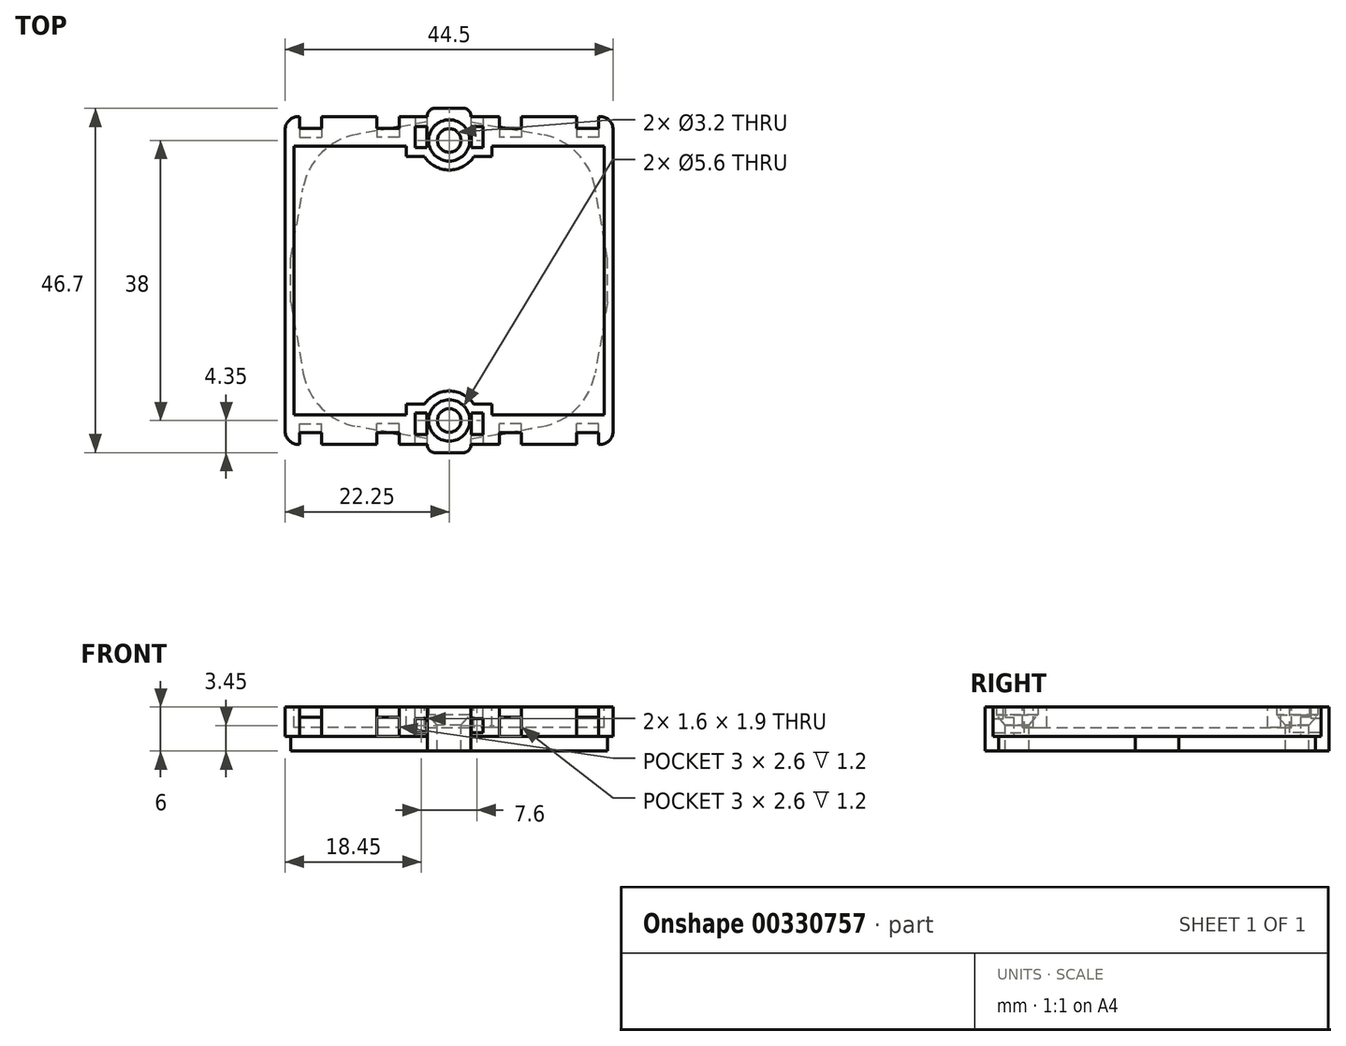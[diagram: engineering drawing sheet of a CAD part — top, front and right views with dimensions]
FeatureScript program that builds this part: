
annotation { "Feature Type Name" : "Feature", "Feature Type Description" : "" }
export const myFeature = defineFeature(function(context is Context, id is Id, definition is map)
    precondition{}
    {
        {
            var Q0;
            Q0=qCreatedBy(makeId("Top.planeOp"),FACE);
            var sketch = newSketch(context, id + "F0", { "sketchPlane" : qUnion([Q0])});
            skLineSegment(sketch, "E0.bottom", {"start": v(4.95, 0) * mm, "end": v(12.45, 0) * mm});
            skLineSegment(sketch, "E0.top", {"start": v(4.95, 44.5) * mm, "end": v(12.45, 44.5) * mm});
            skLineSegment(sketch, "E0.left", {"start": v(0, 1.8) * mm, "end": v(0, 42.7) * mm});
            skLineSegment(sketch, "E0.right", {"start": v(44.5, 1.8) * mm, "end": v(44.5, 42.7) * mm});
            skPoint(sketch, "E1.visualSharp", {"position": v(0, 44.5) * mm});
            skArc(sketch, "E1.filletArc", {"start": v(1.8, 44.5) * mm, "mid": v(0.53, 43.97) * mm, "end": v(0, 42.7) * mm});
            skPoint(sketch, "E2.visualSharp", {"position": v(44.5, 44.5) * mm});
            skArc(sketch, "E2.filletArc", {"start": v(44.5, 42.7) * mm, "mid": v(43.97, 43.97) * mm, "end": v(42.7, 44.5) * mm});
            skPoint(sketch, "E3.visualSharp", {"position": v(44.5, 0) * mm});
            skArc(sketch, "E3.filletArc", {"start": v(42.7, 0) * mm, "mid": v(43.97, 0.53) * mm, "end": v(44.5, 1.8) * mm});
            skPoint(sketch, "E4.visualSharp", {"position": v(0, 0) * mm});
            skArc(sketch, "E4.filletArc", {"start": v(0, 1.8) * mm, "mid": v(0.53, 0.53) * mm, "end": v(1.8, 0) * mm});
            skLineSegment(sketch, "E5.bottom", {"start": v(19.3, 1.1) * mm, "end": v(25.2, 1.1) * mm});
            skLineSegment(sketch, "E5.top", {"start": v(19.3, -1.1) * mm, "end": v(25.2, -1.1) * mm});
            skLineSegment(sketch, "E5.left", {"start": v(19.3, 1.1) * mm, "end": v(19.3, -1.1) * mm});
            skLineSegment(sketch, "E5.right", {"start": v(25.2, 1.1) * mm, "end": v(25.2, -1.1) * mm});
            skPoint(sketch, "E5.middle", {"position": v(22.25, 0) * mm});
            skLineSegment(sketch, "E6.bottom", {"start": v(19.3, 45.6) * mm, "end": v(25.2, 45.6) * mm});
            skLineSegment(sketch, "E6.top", {"start": v(19.3, 43.4) * mm, "end": v(25.2, 43.4) * mm});
            skLineSegment(sketch, "E6.left", {"start": v(19.3, 45.6) * mm, "end": v(19.3, 43.4) * mm});
            skLineSegment(sketch, "E6.right", {"start": v(25.2, 45.6) * mm, "end": v(25.2, 43.4) * mm});
            skPoint(sketch, "E6.middle", {"position": v(22.25, 44.5) * mm});
            skLineSegment(sketch, "E7.bottom", {"start": v(1.8, 0) * mm, "end": v(1.95, 0) * mm});
            skLineSegment(sketch, "E7.top", {"start": v(1.95, 1.6) * mm, "end": v(4.95, 1.6) * mm});
            skLineSegment(sketch, "E7.left", {"start": v(1.95, 0) * mm, "end": v(1.95, 1.6) * mm});
            skLineSegment(sketch, "E7.right", {"start": v(4.95, 0) * mm, "end": v(4.95, 1.6) * mm});
            skPoint(sketch, "E8.oppositeSnap0", {"position": v(3.45, 1.6) * mm});
            skLineSegment(sketch, "E8.top", {"start": v(12.45, 1.6) * mm, "end": v(15.45, 1.6) * mm});
            skLineSegment(sketch, "E8.left", {"start": v(12.45, 0) * mm, "end": v(12.45, 1.6) * mm});
            skLineSegment(sketch, "E8.right", {"start": v(15.45, 0) * mm, "end": v(15.45, 1.6) * mm});
            skLineSegment(sketch, "E9", {"start": v(22.25, 0) * mm, "end": v(22.25, 44.5) * mm, "construction": true});
            skLineSegment(sketch, "E10", {"start": v(44.5, 22.25) * mm, "end": v(0, 22.25) * mm, "construction": true});
            skLineSegment(sketch, "E11.MirrorCS", {"start": v(1.95, 44.5) * mm, "end": v(1.95, 42.9) * mm});
            skLineSegment(sketch, "E12.MirrorCS", {"start": v(1.95, 42.9) * mm, "end": v(4.95, 42.9) * mm});
            skLineSegment(sketch, "E13.MirrorCS", {"start": v(4.95, 44.5) * mm, "end": v(4.95, 42.9) * mm});
            skLineSegment(sketch, "E14.MirrorCS", {"start": v(12.45, 44.5) * mm, "end": v(12.45, 42.9) * mm});
            skLineSegment(sketch, "E15.MirrorCS", {"start": v(12.45, 42.9) * mm, "end": v(15.45, 42.9) * mm});
            skLineSegment(sketch, "E16.MirrorCS", {"start": v(15.45, 44.5) * mm, "end": v(15.45, 42.9) * mm});
            skLineSegment(sketch, "E17.MirrorCS", {"start": v(29.05, 0) * mm, "end": v(29.05, 1.6) * mm});
            skLineSegment(sketch, "E18.MirrorCS", {"start": v(32.05, 1.6) * mm, "end": v(29.05, 1.6) * mm});
            skLineSegment(sketch, "E19.MirrorCS", {"start": v(32.05, 0) * mm, "end": v(32.05, 1.6) * mm});
            skLineSegment(sketch, "E20.MirrorCS", {"start": v(39.55, 0) * mm, "end": v(39.55, 1.6) * mm});
            skLineSegment(sketch, "E21.MirrorCS", {"start": v(42.55, 1.6) * mm, "end": v(39.55, 1.6) * mm});
            skLineSegment(sketch, "E22.MirrorCS", {"start": v(42.55, 0) * mm, "end": v(42.55, 1.6) * mm});
            skLineSegment(sketch, "E23.MirrorCS", {"start": v(42.55, 44.5) * mm, "end": v(42.55, 42.9) * mm});
            skLineSegment(sketch, "E24.MirrorCS", {"start": v(42.55, 42.9) * mm, "end": v(39.55, 42.9) * mm});
            skLineSegment(sketch, "E25.MirrorCS", {"start": v(39.55, 44.5) * mm, "end": v(39.55, 42.9) * mm});
            skLineSegment(sketch, "E26.MirrorCS", {"start": v(32.05, 44.5) * mm, "end": v(32.05, 42.9) * mm});
            skLineSegment(sketch, "E27.MirrorCS", {"start": v(32.05, 42.9) * mm, "end": v(29.05, 42.9) * mm});
            skLineSegment(sketch, "E28.MirrorCS", {"start": v(29.05, 44.5) * mm, "end": v(29.05, 42.9) * mm});
            skLineSegment(sketch, "E29.trimOffspring", {"start": v(15.45, 0) * mm, "end": v(29.05, 0) * mm});
            skLineSegment(sketch, "E30.trimOffspring", {"start": v(32.05, 0) * mm, "end": v(39.55, 0) * mm});
            skLineSegment(sketch, "E31.trimOffspring", {"start": v(32.05, 44.5) * mm, "end": v(39.55, 44.5) * mm});
            skLineSegment(sketch, "E32.trimOffspring", {"start": v(15.45, 44.5) * mm, "end": v(29.05, 44.5) * mm});
            skLineSegment(sketch, "E33", {"start": v(1.8, 44.5) * mm, "end": v(1.95, 44.5) * mm});
            skLineSegment(sketch, "E34", {"start": v(42.55, 44.5) * mm, "end": v(42.7, 44.5) * mm});
            skLineSegment(sketch, "E35", {"start": v(42.55, 0) * mm, "end": v(42.7, 0) * mm});
            skSolve(sketch);
        }
        {
            var Q0;
            Q0 = qSketchRegion(id + "F0", true);
            extrude(context, id + "F1", {"entities" : qUnion([Q0]), "depth" : (4.5 - 1.6) * mm, "offsetDistance" : 25 * mm});
        }
        {
            var Q0;
            Q0=makeQuery(id+"F1.opExtrude","CAP_FACE",FACE,{"disambiguationData":[OSD([sQuery(id+"F0.wireOp",EDGE,"E0.bottom"),sQuery(id+"F0.wireOp",EDGE,"E0.top"),sQuery(id+"F0.wireOp",EDGE,"E0.left"),sQuery(id+"F0.wireOp",EDGE,"E0.right"),sQuery(id+"F0.wireOp",EDGE,"E1.filletArc"),sQuery(id+"F0.wireOp",EDGE,"E2.filletArc"),sQuery(id+"F0.wireOp",EDGE,"E3.filletArc"),sQuery(id+"F0.wireOp",EDGE,"E4.filletArc")])],"isStart":true});
            var sketch = newSketch(context, id + "F2", { "sketchPlane" : qUnion([Q0])});
            skLineSegment(sketch, "E36.bottom", {"start": v(19.3, -0.75) * mm, "end": v(25.2, -0.75) * mm});
            skLineSegment(sketch, "E36.top", {"start": v(19.3, -43.75) * mm, "end": v(25.2, -43.75) * mm});
            skLineSegment(sketch, "E36.left", {"start": v(19.3, -0.75) * mm, "end": v(19.3, -43.75) * mm, "construction": true});
            skLineSegment(sketch, "E36.right", {"start": v(25.2, -0.75) * mm, "end": v(25.2, -43.75) * mm, "construction": true});
            skLineSegment(sketch, "E37.bottom", {"start": v(0.75, -19.3) * mm, "end": v(43.75, -19.3) * mm, "construction": true});
            skLineSegment(sketch, "E37.top", {"start": v(0.75, -25.2) * mm, "end": v(43.75, -25.2) * mm, "construction": true});
            skLineSegment(sketch, "E37.left", {"start": v(0.75, -19.3) * mm, "end": v(0.75, -25.2) * mm});
            skLineSegment(sketch, "E37.right", {"start": v(43.75, -19.3) * mm, "end": v(43.75, -25.2) * mm});
            skPoint(sketch, "E38", {"position": v(22.25, -22.25) * mm});
            skPoint(sketch, "E38.positionSnap0", {"position": v(19.3, -22.25) * mm});
            skPoint(sketch, "E38.positionSnap1", {"position": v(22.25, -25.2) * mm});
            skLineSegment(sketch, "E39", {"start": v(22.25, -22.25) * mm, "end": v(0, 0) * mm, "construction": true});
            skLineSegment(sketch, "E40", {"start": v(22.25, -22.25) * mm, "end": v(43.97, -43.97) * mm, "construction": true});
            skLineSegment(sketch, "E41", {"start": v(22.25, -22.25) * mm, "end": v(41.34, -3.16) * mm, "construction": true});
            skLineSegment(sketch, "E42", {"start": v(22.25, -22.25) * mm, "end": v(5.04, -39.46) * mm, "construction": true});
            skArc(sketch, "E43", {"start": v(9.74, -2.42) * mm, "mid": v(4.93, -4.93) * mm, "end": v(2.42, -9.74) * mm});
            skArc(sketch, "E44", {"start": v(42.08, -9.74) * mm, "mid": v(39.57, -4.93) * mm, "end": v(34.76, -2.42) * mm});
            skArc(sketch, "E45", {"start": v(34.76, -42.08) * mm, "mid": v(39.57, -39.57) * mm, "end": v(42.08, -34.76) * mm});
            skArc(sketch, "E46", {"start": v(2.42, -34.76) * mm, "mid": v(4.93, -39.57) * mm, "end": v(9.74, -42.08) * mm});
            skLineSegment(sketch, "E47", {"start": v(19.3, -0.75) * mm, "end": v(9.74, -2.42) * mm});
            skLineSegment(sketch, "E48", {"start": v(0.75, -19.3) * mm, "end": v(2.42, -9.74) * mm});
            skLineSegment(sketch, "E49", {"start": v(0.75, -25.2) * mm, "end": v(2.42, -34.76) * mm});
            skLineSegment(sketch, "E50", {"start": v(19.3, -43.75) * mm, "end": v(9.74, -42.08) * mm});
            skLineSegment(sketch, "E51", {"start": v(25.2, -43.75) * mm, "end": v(34.76, -42.08) * mm});
            skLineSegment(sketch, "E52", {"start": v(43.75, -25.2) * mm, "end": v(42.08, -34.76) * mm});
            skLineSegment(sketch, "E53", {"start": v(43.75, -19.3) * mm, "end": v(42.08, -9.74) * mm});
            skLineSegment(sketch, "E54", {"start": v(25.2, -0.75) * mm, "end": v(34.76, -2.42) * mm});
            skLineSegment(sketch, "E55.0", {"start": v(19.3, 1.1) * mm, "end": v(25.2, 1.1) * mm});
            skLineSegment(sketch, "E56", {"start": v(25.2, 1.1) * mm, "end": v(25.2, -0.75) * mm});
            skLineSegment(sketch, "E57", {"start": v(19.3, 1.1) * mm, "end": v(19.3, -0.75) * mm});
            skLineSegment(sketch, "E58.0", {"start": v(19.3, -45.6) * mm, "end": v(25.2, -45.6) * mm});
            skLineSegment(sketch, "E59", {"start": v(19.3, -43.75) * mm, "end": v(19.3, -45.6) * mm});
            skLineSegment(sketch, "E60", {"start": v(25.2, -43.75) * mm, "end": v(25.2, -45.6) * mm});
            skSolve(sketch);
        }
        {
            var Q0;
            Q0 = qSketchRegion(id + "F2", true);
            extrude(context, id + "F3", {"entities" : qUnion([Q0]), "operationType" : NewBodyOperationType.ADD, "depth" : 2 * mm, "offsetDistance" : 25 * mm});
        }
        {
            var Q0;
            Q0=makeQuery(id+"F1.opExtrude","CAP_FACE",FACE,{"disambiguationData":[OSD([sQuery(id+"F0.wireOp",EDGE,"E0.bottom"),sQuery(id+"F0.wireOp",EDGE,"E0.top"),sQuery(id+"F0.wireOp",EDGE,"E0.left"),sQuery(id+"F0.wireOp",EDGE,"E0.right"),sQuery(id+"F0.wireOp",EDGE,"E1.filletArc"),sQuery(id+"F0.wireOp",EDGE,"E2.filletArc"),sQuery(id+"F0.wireOp",EDGE,"E3.filletArc"),sQuery(id+"F0.wireOp",EDGE,"E4.filletArc"),sQuery(id+"F0.wireOp",EDGE,"E5.top"),sQuery(id+"F0.wireOp",EDGE,"E5.left"),sQuery(id+"F0.wireOp",EDGE,"E5.right"),sQuery(id+"F0.wireOp",EDGE,"E6.bottom"),sQuery(id+"F0.wireOp",EDGE,"E6.left"),sQuery(id+"F0.wireOp",EDGE,"E6.right")])],"isStart":false});
            var sketch = newSketch(context, id + "F4", { "sketchPlane" : qUnion([Q0])});
            skLineSegment(sketch, "E61", {"start": v(22.25, 45.6) * mm, "end": v(22.25, -1.1) * mm, "construction": true});
            skPoint(sketch, "E62", {"position": v(22.25, 41.25) * mm});
            skPoint(sketch, "E63", {"position": v(22.25, 3.25) * mm});
            skPoint(sketch, "E64", {"position": v(22.25, 22.25) * mm});
            skSolve(sketch);
        }
        {
            var Q0;
            Q0=sQuery(id+"F4.wireOp",VERTEX,"E62");
            var Q1;
            Q1=sQuery(id+"F4.wireOp",VERTEX,"E63");
            var Q2;
            Q2=makeQuery(id+"F1.opExtrude","SWEPT_BODY",BODY,{"disambiguationData":[OSD([sQuery(id+"F0.wireOp",EDGE,"E0.bottom"),sQuery(id+"F0.wireOp",EDGE,"E0.top"),sQuery(id+"F0.wireOp",EDGE,"E0.left"),sQuery(id+"F0.wireOp",EDGE,"E0.right"),sQuery(id+"F0.wireOp",EDGE,"E1.filletArc"),sQuery(id+"F0.wireOp",EDGE,"E2.filletArc"),sQuery(id+"F0.wireOp",EDGE,"E3.filletArc"),sQuery(id+"F0.wireOp",EDGE,"E4.filletArc"),sQuery(id+"F0.wireOp",EDGE,"E5.top"),sQuery(id+"F0.wireOp",EDGE,"E5.left"),sQuery(id+"F0.wireOp",EDGE,"E5.right"),sQuery(id+"F0.wireOp",EDGE,"E6.bottom"),sQuery(id+"F0.wireOp",EDGE,"E6.left"),sQuery(id+"F0.wireOp",EDGE,"E6.right")])]});
            hole(context, id + "F5", {"style" : HoleStyle.C_SINK, "endStyle" : HoleEndStyle.THROUGH, "holeDiameter" : 3.2 * mm, "cSinkDiameter" : 5.6 * mm, "cSinkAngle" : 82 * degree, "majorDiameter" : 5 * mm, "isTappedThrough" : true, "tappedDepth" : 12 * mm, "tapClearance" : 3, "locations" : qUnion([Q0, Q1]), "scope" : qUnion([Q2])});
        }
        {
            var Q0;
            Q0=makeQuery(id+"F1.opExtrude","CAP_FACE",FACE,{"disambiguationData":[OSD([sQuery(id+"F0.wireOp",EDGE,"E0.bottom"),sQuery(id+"F0.wireOp",EDGE,"E0.top"),sQuery(id+"F0.wireOp",EDGE,"E0.left"),sQuery(id+"F0.wireOp",EDGE,"E0.right"),sQuery(id+"F0.wireOp",EDGE,"E1.filletArc"),sQuery(id+"F0.wireOp",EDGE,"E2.filletArc"),sQuery(id+"F0.wireOp",EDGE,"E3.filletArc"),sQuery(id+"F0.wireOp",EDGE,"E4.filletArc"),sQuery(id+"F0.wireOp",EDGE,"E5.top"),sQuery(id+"F0.wireOp",EDGE,"E5.left"),sQuery(id+"F0.wireOp",EDGE,"E5.right"),sQuery(id+"F0.wireOp",EDGE,"E6.bottom"),sQuery(id+"F0.wireOp",EDGE,"E6.left"),sQuery(id+"F0.wireOp",EDGE,"E6.right")])],"isStart":false});
            extrude(context, id + "F6", {"entities" : qUnion([Q0]), "operationType" : NewBodyOperationType.ADD, "depth" : 1.1 * mm, "offsetDistance" : 25 * mm});
        }
        {
            var Q0;
            {var subQ0=sQuery(id+"F0.wireOp",EDGE,"E5.right");var subQ1=sQuery(id+"F0.wireOp",EDGE,"E5.top");Q0=makeQuery(id+"F6.boolean.opBoolean","MERGE",EDGE,{"derivedFrom":[makeQuery(id+"F3.boolean.opBoolean","MERGE",EDGE,{"derivedFrom":[makeQuery(id+"F1.opExtrude","SWEPT_EDGE",EDGE,{"disambiguationData":[OSD([subQ1,subQ0])]}),makeQuery(id+"F3.opExtrude","SWEPT_EDGE",EDGE,{"disambiguationData":[OSD([sQuery(id+"F2.wireOp",EDGE,"E55.0"),sQuery(id+"F2.wireOp",EDGE,"E56")])]})]}),makeQuery(id+"F6.opExtrude","SWEPT_EDGE",EDGE,{"disambiguationData":[OSD([subQ1,subQ0])]})]});}
            var Q1;
            {var subQ0=sQuery(id+"F0.wireOp",EDGE,"E5.left");var subQ1=sQuery(id+"F0.wireOp",EDGE,"E5.top");Q1=makeQuery(id+"F6.boolean.opBoolean","MERGE",EDGE,{"derivedFrom":[makeQuery(id+"F3.boolean.opBoolean","MERGE",EDGE,{"derivedFrom":[makeQuery(id+"F1.opExtrude","SWEPT_EDGE",EDGE,{"disambiguationData":[OSD([subQ1,subQ0])]}),makeQuery(id+"F3.opExtrude","SWEPT_EDGE",EDGE,{"disambiguationData":[OSD([sQuery(id+"F2.wireOp",EDGE,"E55.0"),sQuery(id+"F2.wireOp",EDGE,"E57")])]})]}),makeQuery(id+"F6.opExtrude","SWEPT_EDGE",EDGE,{"disambiguationData":[OSD([subQ1,subQ0])]})]});}
            var Q2;
            {var subQ0=sQuery(id+"F0.wireOp",EDGE,"E6.right");var subQ1=sQuery(id+"F0.wireOp",EDGE,"E6.bottom");Q2=makeQuery(id+"F6.boolean.opBoolean","MERGE",EDGE,{"derivedFrom":[makeQuery(id+"F3.boolean.opBoolean","MERGE",EDGE,{"derivedFrom":[makeQuery(id+"F1.opExtrude","SWEPT_EDGE",EDGE,{"disambiguationData":[OSD([subQ1,subQ0])]}),makeQuery(id+"F3.opExtrude","SWEPT_EDGE",EDGE,{"disambiguationData":[OSD([sQuery(id+"F2.wireOp",EDGE,"E58.0"),sQuery(id+"F2.wireOp",EDGE,"E60")])]})]}),makeQuery(id+"F6.opExtrude","SWEPT_EDGE",EDGE,{"disambiguationData":[OSD([subQ1,subQ0])]})]});}
            var Q3;
            {var subQ0=sQuery(id+"F0.wireOp",EDGE,"E6.left");var subQ1=sQuery(id+"F0.wireOp",EDGE,"E6.bottom");Q3=makeQuery(id+"F6.boolean.opBoolean","MERGE",EDGE,{"derivedFrom":[makeQuery(id+"F3.boolean.opBoolean","MERGE",EDGE,{"derivedFrom":[makeQuery(id+"F1.opExtrude","SWEPT_EDGE",EDGE,{"disambiguationData":[OSD([subQ1,subQ0])]}),makeQuery(id+"F3.opExtrude","SWEPT_EDGE",EDGE,{"disambiguationData":[OSD([sQuery(id+"F2.wireOp",EDGE,"E58.0"),sQuery(id+"F2.wireOp",EDGE,"E59")])]})]}),makeQuery(id+"F6.opExtrude","SWEPT_EDGE",EDGE,{"disambiguationData":[OSD([subQ1,subQ0])]})]});}
            fillet(context, id + "F7", {"entities" : qUnion([Q0, Q1, Q2, Q3]), "tangentPropagation" : true, "radius" : 1 * mm, "defaultsChanged" : true, "vertexSettings" : [], "allowEdgeOverflow" : false});
        }
        {
            var Q0;
            {var subQ0=sQuery(id+"F0.wireOp",EDGE,"E32.trimOffspring");var subQ1=sQuery(id+"F0.wireOp",EDGE,"E28.MirrorCS");var subQ2=sQuery(id+"F0.wireOp",EDGE,"E6.right");var subQ3=sQuery(id+"F0.wireOp",EDGE,"E31.trimOffspring");var subQ4=sQuery(id+"F0.wireOp",EDGE,"E30.trimOffspring");var subQ5=sQuery(id+"F0.wireOp",EDGE,"E29.trimOffspring");var subQ6=sQuery(id+"F0.wireOp",EDGE,"E17.MirrorCS");var subQ7=sQuery(id+"F0.wireOp",EDGE,"E5.right");var subQ8=sQuery(id+"F0.wireOp",EDGE,"E27.MirrorCS");var subQ9=sQuery(id+"F0.wireOp",EDGE,"E26.MirrorCS");var subQ10=sQuery(id+"F0.wireOp",EDGE,"E24.MirrorCS");var subQ11=sQuery(id+"F0.wireOp",EDGE,"E23.MirrorCS");var subQ12=sQuery(id+"F0.wireOp",EDGE,"E3.filletArc");var subQ13=sQuery(id+"F0.wireOp",EDGE,"E2.filletArc");var subQ14=sQuery(id+"F0.wireOp",EDGE,"E25.MirrorCS");var subQ15=sQuery(id+"F0.wireOp",EDGE,"E22.MirrorCS");var subQ16=sQuery(id+"F0.wireOp",EDGE,"E21.MirrorCS");var subQ17=sQuery(id+"F0.wireOp",EDGE,"E0.right");var subQ18=sQuery(id+"F0.wireOp",EDGE,"E18.MirrorCS");var subQ19=sQuery(id+"F0.wireOp",EDGE,"E19.MirrorCS");var subQ20=sQuery(id+"F0.wireOp",EDGE,"E20.MirrorCS");Q0=makeQuery(id+"F3.boolean.opBoolean","SPLIT",FACE,{"disambiguationData":[TD([makeQuery(id+"F1.opExtrude","SWEPT_FACE",FACE,{"disambiguationData":[OSD([subQ17])]})])],"derivedFrom":makeQuery(id+"F1.opExtrude","CAP_FACE",FACE,{"disambiguationData":[OSD([sQuery(id+"F0.wireOp",EDGE,"E0.bottom"),sQuery(id+"F0.wireOp",EDGE,"E0.top"),sQuery(id+"F0.wireOp",EDGE,"E0.left"),subQ17,sQuery(id+"F0.wireOp",EDGE,"E1.filletArc"),subQ13,subQ12,sQuery(id+"F0.wireOp",EDGE,"E4.filletArc"),sQuery(id+"F0.wireOp",EDGE,"E5.top"),sQuery(id+"F0.wireOp",EDGE,"E5.left"),subQ7,sQuery(id+"F0.wireOp",EDGE,"E6.bottom"),sQuery(id+"F0.wireOp",EDGE,"E6.left"),subQ2,sQuery(id+"F0.wireOp",EDGE,"E7.top"),sQuery(id+"F0.wireOp",EDGE,"E7.left"),sQuery(id+"F0.wireOp",EDGE,"E7.right"),sQuery(id+"F0.wireOp",EDGE,"E8.top"),sQuery(id+"F0.wireOp",EDGE,"E8.left"),sQuery(id+"F0.wireOp",EDGE,"E8.right"),sQuery(id+"F0.wireOp",EDGE,"E11.MirrorCS"),sQuery(id+"F0.wireOp",EDGE,"E12.MirrorCS"),sQuery(id+"F0.wireOp",EDGE,"E13.MirrorCS"),sQuery(id+"F0.wireOp",EDGE,"E14.MirrorCS"),sQuery(id+"F0.wireOp",EDGE,"E15.MirrorCS"),sQuery(id+"F0.wireOp",EDGE,"E16.MirrorCS"),subQ6,subQ18,subQ19,subQ20,subQ16,subQ15,subQ11,subQ10,subQ14,subQ9,subQ8,subQ1,subQ5,subQ4,subQ3,subQ0])],"isStart":true})});}
            var sketch = newSketch(context, id + "F8", { "sketchPlane" : qUnion([Q0])});
            skLineSegment(sketch, "E65.bottom", {"start": v(1.95, -42.9) * mm, "end": v(4.95, -42.9) * mm});
            skLineSegment(sketch, "E65.top", {"start": v(1.95, -41.7) * mm, "end": v(4.95, -41.7) * mm});
            skLineSegment(sketch, "E65.left", {"start": v(1.95, -42.9) * mm, "end": v(1.95, -41.7) * mm});
            skLineSegment(sketch, "E65.right", {"start": v(4.95, -42.9) * mm, "end": v(4.95, -41.7) * mm});
            skLineSegment(sketch, "E66.bottom", {"start": v(15.45, -42.9) * mm, "end": v(12.45, -42.9) * mm});
            skLineSegment(sketch, "E66.top", {"start": v(15.45, -41.7) * mm, "end": v(12.45, -41.7) * mm});
            skLineSegment(sketch, "E66.left", {"start": v(15.45, -42.9) * mm, "end": v(15.45, -41.7) * mm});
            skLineSegment(sketch, "E66.right", {"start": v(12.45, -42.9) * mm, "end": v(12.45, -41.7) * mm});
            skLineSegment(sketch, "E67.bottom", {"start": v(1.95, -1.6) * mm, "end": v(4.95, -1.6) * mm});
            skLineSegment(sketch, "E67.top", {"start": v(1.95, -2.8) * mm, "end": v(4.95, -2.8) * mm});
            skLineSegment(sketch, "E67.left", {"start": v(1.95, -1.6) * mm, "end": v(1.95, -2.8) * mm});
            skLineSegment(sketch, "E67.right", {"start": v(4.95, -1.6) * mm, "end": v(4.95, -2.8) * mm});
            skLineSegment(sketch, "E68.bottom", {"start": v(15.45, -1.6) * mm, "end": v(12.45, -1.6) * mm});
            skLineSegment(sketch, "E68.top", {"start": v(15.45, -2.8) * mm, "end": v(12.45, -2.8) * mm});
            skLineSegment(sketch, "E68.left", {"start": v(15.45, -1.6) * mm, "end": v(15.45, -2.8) * mm});
            skLineSegment(sketch, "E68.right", {"start": v(12.45, -1.6) * mm, "end": v(12.45, -2.8) * mm});
            skLineSegment(sketch, "E69.bottom", {"start": v(32.05, -42.9) * mm, "end": v(29.05, -42.9) * mm});
            skLineSegment(sketch, "E69.top", {"start": v(32.05, -41.7) * mm, "end": v(29.05, -41.7) * mm});
            skLineSegment(sketch, "E69.left", {"start": v(32.05, -42.9) * mm, "end": v(32.05, -41.7) * mm});
            skLineSegment(sketch, "E69.right", {"start": v(29.05, -42.9) * mm, "end": v(29.05, -41.7) * mm});
            skLineSegment(sketch, "E70.bottom", {"start": v(42.55, -42.9) * mm, "end": v(39.55, -42.9) * mm});
            skLineSegment(sketch, "E70.top", {"start": v(42.55, -41.7) * mm, "end": v(39.55, -41.7) * mm});
            skLineSegment(sketch, "E70.left", {"start": v(42.55, -42.9) * mm, "end": v(42.55, -41.7) * mm});
            skLineSegment(sketch, "E70.right", {"start": v(39.55, -42.9) * mm, "end": v(39.55, -41.7) * mm});
            skLineSegment(sketch, "E71.bottom", {"start": v(32.05, -1.6) * mm, "end": v(29.05, -1.6) * mm});
            skLineSegment(sketch, "E71.top", {"start": v(32.05, -2.8) * mm, "end": v(29.05, -2.8) * mm});
            skLineSegment(sketch, "E71.left", {"start": v(32.05, -1.6) * mm, "end": v(32.05, -2.8) * mm});
            skLineSegment(sketch, "E71.right", {"start": v(29.05, -1.6) * mm, "end": v(29.05, -2.8) * mm});
            skLineSegment(sketch, "E72.bottom", {"start": v(42.55, -1.6) * mm, "end": v(39.55, -1.6) * mm});
            skLineSegment(sketch, "E72.top", {"start": v(42.55, -2.8) * mm, "end": v(39.55, -2.8) * mm});
            skLineSegment(sketch, "E72.left", {"start": v(42.55, -1.6) * mm, "end": v(42.55, -2.8) * mm});
            skLineSegment(sketch, "E72.right", {"start": v(39.55, -1.6) * mm, "end": v(39.55, -2.8) * mm});
            skSolve(sketch);
        }
        {
            var Q0;
            Q0 = qSketchRegion(id + "F8", true);
            var Q1;
            Q1=makeQuery(id+"F6.opExtrude","CAP_FACE",FACE,{"disambiguationData":[OSD([sQuery(id+"F0.wireOp",EDGE,"E0.bottom"),sQuery(id+"F0.wireOp",EDGE,"E0.top"),sQuery(id+"F0.wireOp",EDGE,"E0.left"),sQuery(id+"F0.wireOp",EDGE,"E0.right"),sQuery(id+"F0.wireOp",EDGE,"E1.filletArc"),sQuery(id+"F0.wireOp",EDGE,"E2.filletArc"),sQuery(id+"F0.wireOp",EDGE,"E3.filletArc"),sQuery(id+"F0.wireOp",EDGE,"E4.filletArc"),sQuery(id+"F0.wireOp",EDGE,"E5.top"),sQuery(id+"F0.wireOp",EDGE,"E5.left"),sQuery(id+"F0.wireOp",EDGE,"E5.right"),sQuery(id+"F0.wireOp",EDGE,"E6.bottom"),sQuery(id+"F0.wireOp",EDGE,"E6.left"),sQuery(id+"F0.wireOp",EDGE,"E6.right"),sQuery(id+"F0.wireOp",EDGE,"E7.top"),sQuery(id+"F0.wireOp",EDGE,"E7.left"),sQuery(id+"F0.wireOp",EDGE,"E7.right"),sQuery(id+"F0.wireOp",EDGE,"E8.top"),sQuery(id+"F0.wireOp",EDGE,"E8.left"),sQuery(id+"F0.wireOp",EDGE,"E8.right"),sQuery(id+"F0.wireOp",EDGE,"E11.MirrorCS"),sQuery(id+"F0.wireOp",EDGE,"E12.MirrorCS"),sQuery(id+"F0.wireOp",EDGE,"E13.MirrorCS"),sQuery(id+"F0.wireOp",EDGE,"E14.MirrorCS"),sQuery(id+"F0.wireOp",EDGE,"E15.MirrorCS"),sQuery(id+"F0.wireOp",EDGE,"E16.MirrorCS"),sQuery(id+"F0.wireOp",EDGE,"E17.MirrorCS"),sQuery(id+"F0.wireOp",EDGE,"E18.MirrorCS"),sQuery(id+"F0.wireOp",EDGE,"E19.MirrorCS"),sQuery(id+"F0.wireOp",EDGE,"E20.MirrorCS"),sQuery(id+"F0.wireOp",EDGE,"E21.MirrorCS"),sQuery(id+"F0.wireOp",EDGE,"E22.MirrorCS"),sQuery(id+"F0.wireOp",EDGE,"E23.MirrorCS"),sQuery(id+"F0.wireOp",EDGE,"E24.MirrorCS"),sQuery(id+"F0.wireOp",EDGE,"E25.MirrorCS"),sQuery(id+"F0.wireOp",EDGE,"E26.MirrorCS"),sQuery(id+"F0.wireOp",EDGE,"E27.MirrorCS"),sQuery(id+"F0.wireOp",EDGE,"E28.MirrorCS"),sQuery(id+"F0.wireOp",EDGE,"E29.trimOffspring"),sQuery(id+"F0.wireOp",EDGE,"E30.trimOffspring"),sQuery(id+"F0.wireOp",EDGE,"E31.trimOffspring"),sQuery(id+"F0.wireOp",EDGE,"E32.trimOffspring")])],"isStart":false});
            var Q2;
            Q2=makeQuery(id+"F3.opExtrude","CAP_FACE",FACE,{"disambiguationData":[OSD([sQuery(id+"F2.wireOp",EDGE,"E37.left"),sQuery(id+"F2.wireOp",EDGE,"E37.right"),sQuery(id+"F2.wireOp",EDGE,"E43"),sQuery(id+"F2.wireOp",EDGE,"E44"),sQuery(id+"F2.wireOp",EDGE,"E45"),sQuery(id+"F2.wireOp",EDGE,"E46"),sQuery(id+"F2.wireOp",EDGE,"E47"),sQuery(id+"F2.wireOp",EDGE,"E48"),sQuery(id+"F2.wireOp",EDGE,"E49"),sQuery(id+"F2.wireOp",EDGE,"E50"),sQuery(id+"F2.wireOp",EDGE,"E51"),sQuery(id+"F2.wireOp",EDGE,"E52"),sQuery(id+"F2.wireOp",EDGE,"E53"),sQuery(id+"F2.wireOp",EDGE,"E54"),sQuery(id+"F2.wireOp",EDGE,"E55.0"),sQuery(id+"F2.wireOp",EDGE,"E56"),sQuery(id+"F2.wireOp",EDGE,"E57"),sQuery(id+"F2.wireOp",EDGE,"E58.0"),sQuery(id+"F2.wireOp",EDGE,"E59"),sQuery(id+"F2.wireOp",EDGE,"E60")])],"isStart":false});
            extrude(context, id + "F9", {"entities" : qUnion([Q0]), "operationType" : NewBodyOperationType.REMOVE, "endBound" : BoundingType.UP_TO_SURFACE, "oppositeDirection" : true, "depth" : 1 * mm, "endBoundEntityFace" : qUnion([Q1]), "hasOffset" : true, "offsetDistance" : 1.4 * mm});
        }
        {
            var Q0;
            Q0=makeQuery(id+"F6.opExtrude","CAP_FACE",FACE,{"disambiguationData":[OSD([sQuery(id+"F0.wireOp",EDGE,"E0.bottom"),sQuery(id+"F0.wireOp",EDGE,"E0.top"),sQuery(id+"F0.wireOp",EDGE,"E0.left"),sQuery(id+"F0.wireOp",EDGE,"E0.right"),sQuery(id+"F0.wireOp",EDGE,"E1.filletArc"),sQuery(id+"F0.wireOp",EDGE,"E2.filletArc"),sQuery(id+"F0.wireOp",EDGE,"E3.filletArc"),sQuery(id+"F0.wireOp",EDGE,"E4.filletArc"),sQuery(id+"F0.wireOp",EDGE,"E5.top"),sQuery(id+"F0.wireOp",EDGE,"E5.left"),sQuery(id+"F0.wireOp",EDGE,"E5.right"),sQuery(id+"F0.wireOp",EDGE,"E6.bottom"),sQuery(id+"F0.wireOp",EDGE,"E6.left"),sQuery(id+"F0.wireOp",EDGE,"E6.right"),sQuery(id+"F0.wireOp",EDGE,"E7.top"),sQuery(id+"F0.wireOp",EDGE,"E7.left"),sQuery(id+"F0.wireOp",EDGE,"E7.right"),sQuery(id+"F0.wireOp",EDGE,"E8.top"),sQuery(id+"F0.wireOp",EDGE,"E8.left"),sQuery(id+"F0.wireOp",EDGE,"E8.right"),sQuery(id+"F0.wireOp",EDGE,"E11.MirrorCS"),sQuery(id+"F0.wireOp",EDGE,"E12.MirrorCS"),sQuery(id+"F0.wireOp",EDGE,"E13.MirrorCS"),sQuery(id+"F0.wireOp",EDGE,"E14.MirrorCS"),sQuery(id+"F0.wireOp",EDGE,"E15.MirrorCS"),sQuery(id+"F0.wireOp",EDGE,"E16.MirrorCS"),sQuery(id+"F0.wireOp",EDGE,"E17.MirrorCS"),sQuery(id+"F0.wireOp",EDGE,"E18.MirrorCS"),sQuery(id+"F0.wireOp",EDGE,"E19.MirrorCS"),sQuery(id+"F0.wireOp",EDGE,"E20.MirrorCS"),sQuery(id+"F0.wireOp",EDGE,"E21.MirrorCS"),sQuery(id+"F0.wireOp",EDGE,"E22.MirrorCS"),sQuery(id+"F0.wireOp",EDGE,"E23.MirrorCS"),sQuery(id+"F0.wireOp",EDGE,"E24.MirrorCS"),sQuery(id+"F0.wireOp",EDGE,"E25.MirrorCS"),sQuery(id+"F0.wireOp",EDGE,"E26.MirrorCS"),sQuery(id+"F0.wireOp",EDGE,"E27.MirrorCS"),sQuery(id+"F0.wireOp",EDGE,"E28.MirrorCS"),sQuery(id+"F0.wireOp",EDGE,"E29.trimOffspring"),sQuery(id+"F0.wireOp",EDGE,"E30.trimOffspring"),sQuery(id+"F0.wireOp",EDGE,"E31.trimOffspring"),sQuery(id+"F0.wireOp",EDGE,"E32.trimOffspring")])],"isStart":false});
            var sketch = newSketch(context, id + "F10", { "sketchPlane" : qUnion([Q0])});
            skLineSegment(sketch, "E73.top", {"start": v(19.25, 4.25) * mm, "end": v(17.65, 4.25) * mm});
            skLineSegment(sketch, "E73.left", {"start": v(19.25, 1.55) * mm, "end": v(19.25, 4.25) * mm});
            skLineSegment(sketch, "E73.right", {"start": v(17.65, 1.55) * mm, "end": v(17.65, 4.25) * mm});
            skLineSegment(sketch, "E74", {"start": v(22.25, 45.6) * mm, "end": v(22.25, -1.1) * mm, "construction": true});
            skLineSegment(sketch, "E75", {"start": v(44.5, 22.25) * mm, "end": v(0, 22.25) * mm, "construction": true});
            skLineSegment(sketch, "E76.top", {"start": v(17.65, 0) * mm, "end": v(19.25, 0) * mm});
            skLineSegment(sketch, "E76.left", {"start": v(17.65, 1.55) * mm, "end": v(17.65, 0) * mm});
            skLineSegment(sketch, "E76.right", {"start": v(19.25, 1.55) * mm, "end": v(19.25, 0) * mm});
            skLineSegment(sketch, "E77.MirrorCS", {"start": v(19.25, 40.25) * mm, "end": v(17.65, 40.25) * mm});
            skLineSegment(sketch, "E78.MirrorCS", {"start": v(19.25, 42.95) * mm, "end": v(19.25, 40.25) * mm});
            skLineSegment(sketch, "E79.MirrorCS", {"start": v(19.25, 42.95) * mm, "end": v(19.25, 44.5) * mm});
            skLineSegment(sketch, "E80.MirrorCS", {"start": v(17.65, 42.95) * mm, "end": v(17.65, 40.25) * mm});
            skLineSegment(sketch, "E81.MirrorCS", {"start": v(17.65, 42.95) * mm, "end": v(17.65, 44.5) * mm});
            skLineSegment(sketch, "E82.MirrorCS", {"start": v(17.65, 44.5) * mm, "end": v(19.25, 44.5) * mm});
            skLineSegment(sketch, "E83.MirrorCS", {"start": v(25.25, 1.55) * mm, "end": v(25.25, 0) * mm});
            skLineSegment(sketch, "E84.MirrorCS", {"start": v(25.25, 1.55) * mm, "end": v(25.25, 4.25) * mm});
            skLineSegment(sketch, "E85.MirrorCS", {"start": v(25.25, 4.25) * mm, "end": v(26.85, 4.25) * mm});
            skLineSegment(sketch, "E86.MirrorCS", {"start": v(26.85, 1.55) * mm, "end": v(26.85, 4.25) * mm});
            skLineSegment(sketch, "E87.MirrorCS", {"start": v(26.85, 1.55) * mm, "end": v(26.85, 0) * mm});
            skLineSegment(sketch, "E88.MirrorCS", {"start": v(26.85, 0) * mm, "end": v(25.25, 0) * mm});
            skLineSegment(sketch, "E89.MirrorCS", {"start": v(25.25, 40.25) * mm, "end": v(26.85, 40.25) * mm});
            skLineSegment(sketch, "E90.MirrorCS", {"start": v(26.85, 42.95) * mm, "end": v(26.85, 40.25) * mm});
            skLineSegment(sketch, "E91.MirrorCS", {"start": v(26.85, 42.95) * mm, "end": v(26.85, 44.5) * mm});
            skLineSegment(sketch, "E92.MirrorCS", {"start": v(26.85, 44.5) * mm, "end": v(25.25, 44.5) * mm});
            skLineSegment(sketch, "E93.MirrorCS", {"start": v(25.25, 42.95) * mm, "end": v(25.25, 44.5) * mm});
            skLineSegment(sketch, "E94.MirrorCS", {"start": v(25.25, 42.95) * mm, "end": v(25.25, 40.25) * mm});
            skLineSegment(sketch, "E95.MirrorCS", {"start": v(17.65, 42.95) * mm, "end": v(19.25, 42.95) * mm});
            skPoint(sketch, "E96.MirrorCS.end.orphan", {"position": v(25.25, 42.95) * mm});
            skPoint(sketch, "E96.MirrorCS.start.orphan", {"position": v(26.85, 42.95) * mm});
            skPoint(sketch, "E97.MirrorCS.end.orphan", {"position": v(19.25, 42.95) * mm});
            skPoint(sketch, "E97.MirrorCS.start.orphan", {"position": v(17.65, 42.95) * mm});
            skPoint(sketch, "E98.MirrorCS.end.orphan", {"position": v(25.25, 1.55) * mm});
            skPoint(sketch, "E98.MirrorCS.start.orphan", {"position": v(26.85, 1.55) * mm});
            skSolve(sketch);
        }
        {
            var Q0;
            Q0 = qSketchRegion(id + "F10", true);
            extrude(context, id + "F11", {"entities" : qUnion([Q0]), "operationType" : NewBodyOperationType.REMOVE, "oppositeDirection" : true, "depth" : 3.5 * mm, "offsetDistance" : 25 * mm});
        }
        {
            var Q0;
            Q0=makeQuery(id+"F6.opExtrude","CAP_FACE",FACE,{"disambiguationData":[OSD([sQuery(id+"F0.wireOp",EDGE,"E0.bottom"),sQuery(id+"F0.wireOp",EDGE,"E0.top"),sQuery(id+"F0.wireOp",EDGE,"E0.left"),sQuery(id+"F0.wireOp",EDGE,"E0.right"),sQuery(id+"F0.wireOp",EDGE,"E1.filletArc"),sQuery(id+"F0.wireOp",EDGE,"E2.filletArc"),sQuery(id+"F0.wireOp",EDGE,"E3.filletArc"),sQuery(id+"F0.wireOp",EDGE,"E4.filletArc"),sQuery(id+"F0.wireOp",EDGE,"E5.top"),sQuery(id+"F0.wireOp",EDGE,"E5.left"),sQuery(id+"F0.wireOp",EDGE,"E5.right"),sQuery(id+"F0.wireOp",EDGE,"E6.bottom"),sQuery(id+"F0.wireOp",EDGE,"E6.left"),sQuery(id+"F0.wireOp",EDGE,"E6.right"),sQuery(id+"F0.wireOp",EDGE,"E7.top"),sQuery(id+"F0.wireOp",EDGE,"E7.left"),sQuery(id+"F0.wireOp",EDGE,"E7.right"),sQuery(id+"F0.wireOp",EDGE,"E8.top"),sQuery(id+"F0.wireOp",EDGE,"E8.left"),sQuery(id+"F0.wireOp",EDGE,"E8.right"),sQuery(id+"F0.wireOp",EDGE,"E11.MirrorCS"),sQuery(id+"F0.wireOp",EDGE,"E12.MirrorCS"),sQuery(id+"F0.wireOp",EDGE,"E13.MirrorCS"),sQuery(id+"F0.wireOp",EDGE,"E14.MirrorCS"),sQuery(id+"F0.wireOp",EDGE,"E15.MirrorCS"),sQuery(id+"F0.wireOp",EDGE,"E16.MirrorCS"),sQuery(id+"F0.wireOp",EDGE,"E17.MirrorCS"),sQuery(id+"F0.wireOp",EDGE,"E18.MirrorCS"),sQuery(id+"F0.wireOp",EDGE,"E19.MirrorCS"),sQuery(id+"F0.wireOp",EDGE,"E20.MirrorCS"),sQuery(id+"F0.wireOp",EDGE,"E21.MirrorCS"),sQuery(id+"F0.wireOp",EDGE,"E22.MirrorCS"),sQuery(id+"F0.wireOp",EDGE,"E23.MirrorCS"),sQuery(id+"F0.wireOp",EDGE,"E24.MirrorCS"),sQuery(id+"F0.wireOp",EDGE,"E25.MirrorCS"),sQuery(id+"F0.wireOp",EDGE,"E26.MirrorCS"),sQuery(id+"F0.wireOp",EDGE,"E27.MirrorCS"),sQuery(id+"F0.wireOp",EDGE,"E28.MirrorCS"),sQuery(id+"F0.wireOp",EDGE,"E29.trimOffspring"),sQuery(id+"F0.wireOp",EDGE,"E30.trimOffspring"),sQuery(id+"F0.wireOp",EDGE,"E31.trimOffspring"),sQuery(id+"F0.wireOp",EDGE,"E32.trimOffspring")])],"isStart":false});
            var sketch = newSketch(context, id + "F12", { "sketchPlane" : qUnion([Q0])});
            skLineSegment(sketch, "E99", {"start": v(0, 22.25) * mm, "end": v(44.5, 22.25) * mm, "construction": true});
            skLineSegment(sketch, "E100", {"start": v(22.25, 45.6) * mm, "end": v(22.25, -1.1) * mm, "construction": true});
            skLineSegment(sketch, "E101.bottom", {"start": v(26.85, 0) * mm, "end": v(25.25, 0) * mm});
            skLineSegment(sketch, "E101.top", {"start": v(26.85, 1.35) * mm, "end": v(25.25, 1.35) * mm});
            skLineSegment(sketch, "E101.left", {"start": v(26.85, 0) * mm, "end": v(26.85, 1.35) * mm});
            skLineSegment(sketch, "E101.right", {"start": v(25.25, 0) * mm, "end": v(25.25, 1.35) * mm});
            skLineSegment(sketch, "E102.MirrorCS", {"start": v(17.65, 0) * mm, "end": v(19.25, 0) * mm});
            skLineSegment(sketch, "E103.MirrorCS", {"start": v(17.65, 0) * mm, "end": v(17.65, 1.35) * mm});
            skLineSegment(sketch, "E104.MirrorCS", {"start": v(17.65, 1.35) * mm, "end": v(19.25, 1.35) * mm});
            skLineSegment(sketch, "E105.MirrorCS", {"start": v(19.25, 0) * mm, "end": v(19.25, 1.35) * mm});
            skLineSegment(sketch, "E106.MirrorCS", {"start": v(26.85, 43.15) * mm, "end": v(25.25, 43.15) * mm});
            skLineSegment(sketch, "E107.MirrorCS", {"start": v(26.85, 44.5) * mm, "end": v(26.85, 43.15) * mm});
            skLineSegment(sketch, "E108.MirrorCS", {"start": v(25.25, 44.5) * mm, "end": v(25.25, 43.15) * mm});
            skLineSegment(sketch, "E109.MirrorCS", {"start": v(26.85, 44.5) * mm, "end": v(25.25, 44.5) * mm});
            skLineSegment(sketch, "E110.MirrorCS", {"start": v(19.25, 44.5) * mm, "end": v(19.25, 43.15) * mm});
            skLineSegment(sketch, "E111.MirrorCS", {"start": v(17.65, 44.5) * mm, "end": v(19.25, 44.5) * mm});
            skLineSegment(sketch, "E112.MirrorCS", {"start": v(17.65, 44.5) * mm, "end": v(17.65, 43.15) * mm});
            skLineSegment(sketch, "E113.MirrorCS", {"start": v(17.65, 43.15) * mm, "end": v(19.25, 43.15) * mm});
            skSolve(sketch);
        }
        {
            var Q0;
            Q0 = qSketchRegion(id + "F12", true);
            extrude(context, id + "F13", {"entities" : qUnion([Q0]), "operationType" : NewBodyOperationType.ADD, "oppositeDirection" : true, "depth" : 1.6 * mm, "offsetDistance" : 25 * mm});
        }
        {
            var Q0;
            Q0=makeQuery(id+"F13.boolean.opBoolean","MERGE",FACE,{"derivedFrom":[makeQuery(id+"F6.opExtrude","CAP_FACE",FACE,{"disambiguationData":[OSD([sQuery(id+"F0.wireOp",EDGE,"E0.bottom"),sQuery(id+"F0.wireOp",EDGE,"E0.top"),sQuery(id+"F0.wireOp",EDGE,"E0.left"),sQuery(id+"F0.wireOp",EDGE,"E0.right"),sQuery(id+"F0.wireOp",EDGE,"E1.filletArc"),sQuery(id+"F0.wireOp",EDGE,"E2.filletArc"),sQuery(id+"F0.wireOp",EDGE,"E3.filletArc"),sQuery(id+"F0.wireOp",EDGE,"E4.filletArc"),sQuery(id+"F0.wireOp",EDGE,"E5.top"),sQuery(id+"F0.wireOp",EDGE,"E5.left"),sQuery(id+"F0.wireOp",EDGE,"E5.right"),sQuery(id+"F0.wireOp",EDGE,"E6.bottom"),sQuery(id+"F0.wireOp",EDGE,"E6.left"),sQuery(id+"F0.wireOp",EDGE,"E6.right"),sQuery(id+"F0.wireOp",EDGE,"E7.bottom"),sQuery(id+"F0.wireOp",EDGE,"E7.top"),sQuery(id+"F0.wireOp",EDGE,"E7.left"),sQuery(id+"F0.wireOp",EDGE,"E7.right"),sQuery(id+"F0.wireOp",EDGE,"E8.top"),sQuery(id+"F0.wireOp",EDGE,"E8.left"),sQuery(id+"F0.wireOp",EDGE,"E8.right"),sQuery(id+"F0.wireOp",EDGE,"E11.MirrorCS"),sQuery(id+"F0.wireOp",EDGE,"E12.MirrorCS"),sQuery(id+"F0.wireOp",EDGE,"E13.MirrorCS"),sQuery(id+"F0.wireOp",EDGE,"E14.MirrorCS"),sQuery(id+"F0.wireOp",EDGE,"E15.MirrorCS"),sQuery(id+"F0.wireOp",EDGE,"E16.MirrorCS"),sQuery(id+"F0.wireOp",EDGE,"E17.MirrorCS"),sQuery(id+"F0.wireOp",EDGE,"E18.MirrorCS"),sQuery(id+"F0.wireOp",EDGE,"E19.MirrorCS"),sQuery(id+"F0.wireOp",EDGE,"E20.MirrorCS"),sQuery(id+"F0.wireOp",EDGE,"E21.MirrorCS"),sQuery(id+"F0.wireOp",EDGE,"E22.MirrorCS"),sQuery(id+"F0.wireOp",EDGE,"E23.MirrorCS"),sQuery(id+"F0.wireOp",EDGE,"E24.MirrorCS"),sQuery(id+"F0.wireOp",EDGE,"E25.MirrorCS"),sQuery(id+"F0.wireOp",EDGE,"E26.MirrorCS"),sQuery(id+"F0.wireOp",EDGE,"E27.MirrorCS"),sQuery(id+"F0.wireOp",EDGE,"E28.MirrorCS"),sQuery(id+"F0.wireOp",EDGE,"E29.trimOffspring"),sQuery(id+"F0.wireOp",EDGE,"E30.trimOffspring"),sQuery(id+"F0.wireOp",EDGE,"E31.trimOffspring"),sQuery(id+"F0.wireOp",EDGE,"E32.trimOffspring"),sQuery(id+"F0.wireOp",EDGE,"E33"),sQuery(id+"F0.wireOp",EDGE,"E34"),sQuery(id+"F0.wireOp",EDGE,"E35")])],"isStart":false}),makeQuery(id+"F13.opExtrude","CAP_FACE",FACE,{"disambiguationData":[OSD([sQuery(id+"F12.wireOp",EDGE,"E101.bottom"),sQuery(id+"F12.wireOp",EDGE,"E101.top"),sQuery(id+"F12.wireOp",EDGE,"E101.left"),sQuery(id+"F12.wireOp",EDGE,"E101.right")])],"isStart":true}),makeQuery(id+"F13.opExtrude","CAP_FACE",FACE,{"disambiguationData":[OSD([sQuery(id+"F12.wireOp",EDGE,"E102.MirrorCS"),sQuery(id+"F12.wireOp",EDGE,"E103.MirrorCS"),sQuery(id+"F12.wireOp",EDGE,"E104.MirrorCS"),sQuery(id+"F12.wireOp",EDGE,"E105.MirrorCS")])],"isStart":true}),makeQuery(id+"F13.opExtrude","CAP_FACE",FACE,{"disambiguationData":[OSD([sQuery(id+"F12.wireOp",EDGE,"E106.MirrorCS"),sQuery(id+"F12.wireOp",EDGE,"E107.MirrorCS"),sQuery(id+"F12.wireOp",EDGE,"E108.MirrorCS"),sQuery(id+"F12.wireOp",EDGE,"E109.MirrorCS")])],"isStart":true}),makeQuery(id+"F13.opExtrude","CAP_FACE",FACE,{"disambiguationData":[OSD([sQuery(id+"F12.wireOp",EDGE,"E110.MirrorCS"),sQuery(id+"F12.wireOp",EDGE,"E111.MirrorCS"),sQuery(id+"F12.wireOp",EDGE,"E112.MirrorCS"),sQuery(id+"F12.wireOp",EDGE,"E113.MirrorCS")])],"isStart":true})]});
            var sketch = newSketch(context, id + "F14", { "sketchPlane" : qUnion([Q0])});
            skLineSegment(sketch, "E114.bottom", {"start": v(1.2, 40.5) * mm, "end": v(16.45, 40.5) * mm});
            skLineSegment(sketch, "E114.left", {"start": v(1.2, 40.5) * mm, "end": v(1.2, 22.25) * mm});
            skLineSegment(sketch, "E114.right", {"start": v(43.3, 40.5) * mm, "end": v(43.3, 22.25) * mm});
            skArc(sketch, "E115.0", {"start": v(18.9, 39.05) * mm, "mid": v(22.25, 37.25) * mm, "end": v(25.6, 39.05) * mm});
            skLineSegment(sketch, "E116.0", {"start": v(18.9, 39.05) * mm, "end": v(16.45, 39.05) * mm});
            skLineSegment(sketch, "E116.1", {"start": v(16.45, 40.5) * mm, "end": v(16.45, 39.05) * mm});
            skLineSegment(sketch, "E117.0", {"start": v(28.05, 40.5) * mm, "end": v(28.05, 39.05) * mm});
            skLineSegment(sketch, "E117.1", {"start": v(25.6, 39.05) * mm, "end": v(28.05, 39.05) * mm});
            skLineSegment(sketch, "E118.trimOffspring", {"start": v(28.05, 40.5) * mm, "end": v(43.3, 40.5) * mm});
            skLineSegment(sketch, "E119", {"start": v(0, 22.25) * mm, "end": v(44.5, 22.25) * mm, "construction": true});
            skLineSegment(sketch, "E120.MirrorCS", {"start": v(1.2, 4) * mm, "end": v(1.2, 22.25) * mm});
            skLineSegment(sketch, "E121.MirrorCS", {"start": v(1.2, 4) * mm, "end": v(16.45, 4) * mm});
            skLineSegment(sketch, "E122.MirrorCS", {"start": v(16.45, 4) * mm, "end": v(16.45, 5.45) * mm});
            skLineSegment(sketch, "E123.MirrorCS", {"start": v(18.9, 5.45) * mm, "end": v(16.45, 5.45) * mm});
            skArc(sketch, "E124.MirrorCS", {"start": v(18.9, 5.45) * mm, "mid": v(22.25, 7.25) * mm, "end": v(25.6, 5.45) * mm});
            skLineSegment(sketch, "E125.MirrorCS", {"start": v(25.6, 5.45) * mm, "end": v(28.05, 5.45) * mm});
            skLineSegment(sketch, "E126.MirrorCS", {"start": v(28.05, 4) * mm, "end": v(28.05, 5.45) * mm});
            skLineSegment(sketch, "E127.MirrorCS", {"start": v(28.05, 4) * mm, "end": v(43.3, 4) * mm});
            skLineSegment(sketch, "E128.MirrorCS", {"start": v(43.3, 4) * mm, "end": v(43.3, 22.25) * mm});
            skSolve(sketch);
        }
        {
            var Q0;
            Q0=makeQuery(id+"F14.imprint","IMPRINT",FACE,{"disambiguationData":[TD([[makeQuery(id+"F14.imprint","IMPRINT",EDGE,{"derivedFrom":sQuery(id+"F14.wireOp",EDGE,"E114.bottom")}),-1.0]])]});
            var Q1;
            {var subQ7=sQuery(id+"F0.wireOp",EDGE,"E13.MirrorCS");var subQ8=sQuery(id+"F0.wireOp",EDGE,"E33");var subQ9=sQuery(id+"F0.wireOp",EDGE,"E0.bottom");var subQ10=sQuery(id+"F0.wireOp",EDGE,"E12.MirrorCS");var subQ11=sQuery(id+"F0.wireOp",EDGE,"E8.left");var subQ12=sQuery(id+"F0.wireOp",EDGE,"E1.filletArc");var subQ13=sQuery(id+"F0.wireOp",EDGE,"E7.top");var subQ14=sQuery(id+"F0.wireOp",EDGE,"E15.MirrorCS");var subQ15=sQuery(id+"F0.wireOp",EDGE,"E0.left");var subQ16=sQuery(id+"F0.wireOp",EDGE,"E14.MirrorCS");var subQ17=sQuery(id+"F0.wireOp",EDGE,"E0.top");var subQ18=sQuery(id+"F0.wireOp",EDGE,"E11.MirrorCS");var subQ19=sQuery(id+"F0.wireOp",EDGE,"E4.filletArc");var subQ20=sQuery(id+"F0.wireOp",EDGE,"E8.top");var subQ21=sQuery(id+"F0.wireOp",EDGE,"E7.bottom");var subQ22=sQuery(id+"F0.wireOp",EDGE,"E7.left");var subQ23=sQuery(id+"F0.wireOp",EDGE,"E7.right");Q1=makeQuery(id+"F3.boolean.opBoolean","SPLIT",FACE,{"disambiguationData":[TD([makeQuery(id+"F1.opExtrude","SWEPT_FACE",FACE,{"disambiguationData":[OSD([subQ9])]})])],"derivedFrom":makeQuery(id+"F1.opExtrude","CAP_FACE",FACE,{"disambiguationData":[OSD([subQ9,subQ17,subQ15,sQuery(id+"F0.wireOp",EDGE,"E0.right"),subQ12,sQuery(id+"F0.wireOp",EDGE,"E2.filletArc"),sQuery(id+"F0.wireOp",EDGE,"E3.filletArc"),subQ19,sQuery(id+"F0.wireOp",EDGE,"E5.top"),sQuery(id+"F0.wireOp",EDGE,"E5.left"),sQuery(id+"F0.wireOp",EDGE,"E5.right"),sQuery(id+"F0.wireOp",EDGE,"E6.bottom"),sQuery(id+"F0.wireOp",EDGE,"E6.left"),sQuery(id+"F0.wireOp",EDGE,"E6.right"),subQ21,subQ13,subQ22,subQ23,subQ20,subQ11,sQuery(id+"F0.wireOp",EDGE,"E8.right"),subQ18,subQ10,subQ7,subQ16,subQ14,sQuery(id+"F0.wireOp",EDGE,"E16.MirrorCS"),sQuery(id+"F0.wireOp",EDGE,"E17.MirrorCS"),sQuery(id+"F0.wireOp",EDGE,"E18.MirrorCS"),sQuery(id+"F0.wireOp",EDGE,"E19.MirrorCS"),sQuery(id+"F0.wireOp",EDGE,"E20.MirrorCS"),sQuery(id+"F0.wireOp",EDGE,"E21.MirrorCS"),sQuery(id+"F0.wireOp",EDGE,"E22.MirrorCS"),sQuery(id+"F0.wireOp",EDGE,"E23.MirrorCS"),sQuery(id+"F0.wireOp",EDGE,"E24.MirrorCS"),sQuery(id+"F0.wireOp",EDGE,"E25.MirrorCS"),sQuery(id+"F0.wireOp",EDGE,"E26.MirrorCS"),sQuery(id+"F0.wireOp",EDGE,"E27.MirrorCS"),sQuery(id+"F0.wireOp",EDGE,"E28.MirrorCS"),sQuery(id+"F0.wireOp",EDGE,"E29.trimOffspring"),sQuery(id+"F0.wireOp",EDGE,"E30.trimOffspring"),sQuery(id+"F0.wireOp",EDGE,"E31.trimOffspring"),sQuery(id+"F0.wireOp",EDGE,"E32.trimOffspring"),subQ8,sQuery(id+"F0.wireOp",EDGE,"E34"),sQuery(id+"F0.wireOp",EDGE,"E35")])],"isStart":true})});}
            extrude(context, id + "F15", {"entities" : qUnion([Q0]), "operationType" : NewBodyOperationType.REMOVE, "endBound" : BoundingType.UP_TO_SURFACE, "oppositeDirection" : true, "depth" : 25 * mm, "endBoundEntityFace" : qUnion([Q1]), "hasOffset" : true, "offsetDistance" : 1.2 * mm});
        }
    });
